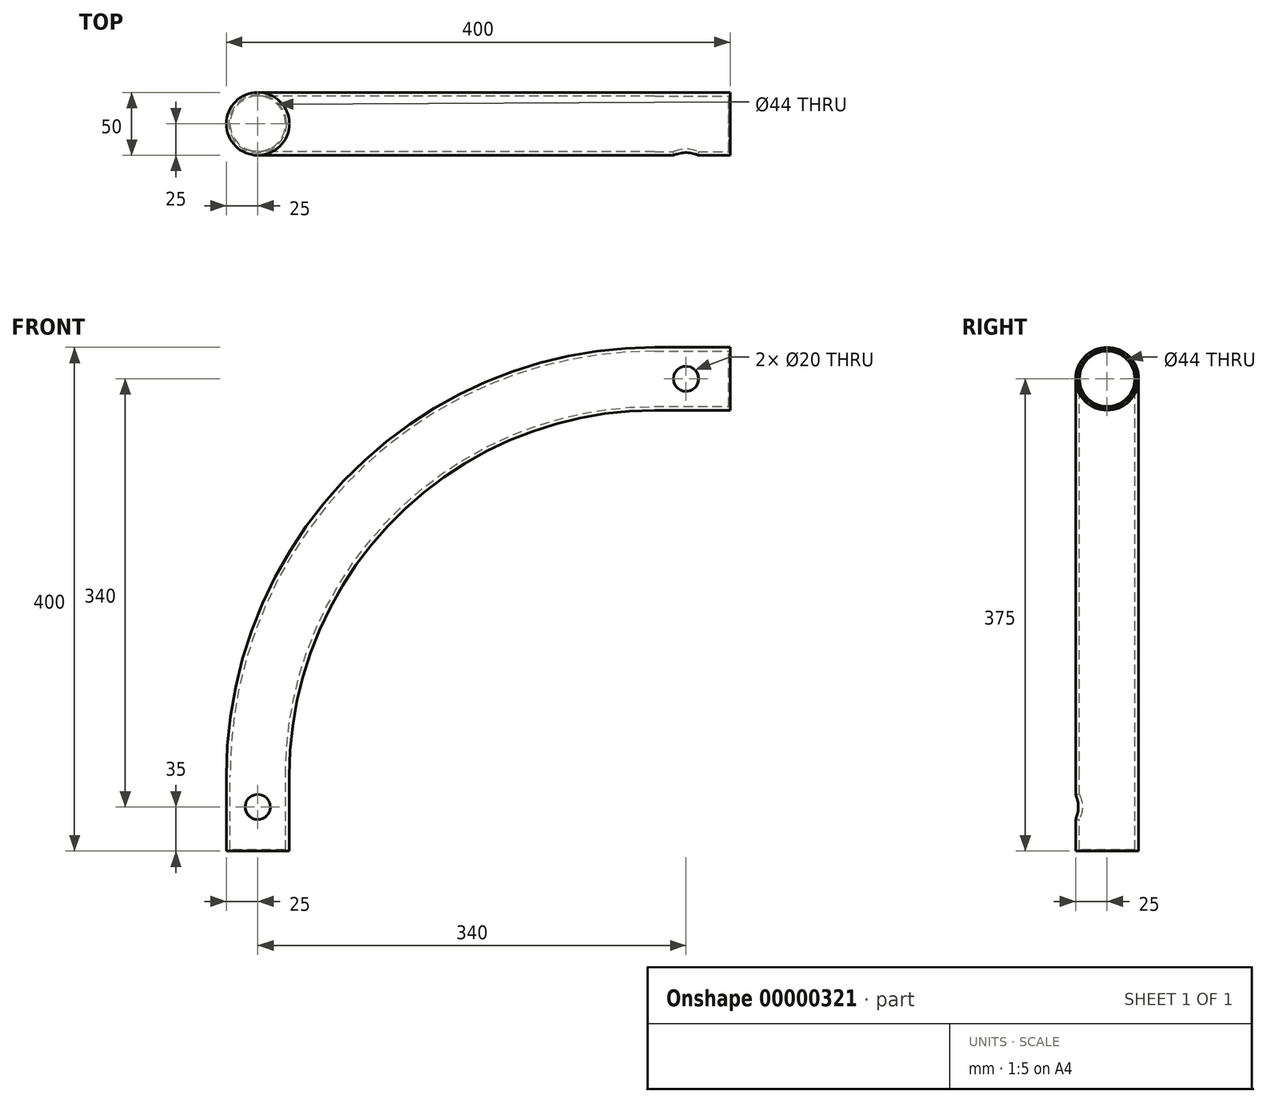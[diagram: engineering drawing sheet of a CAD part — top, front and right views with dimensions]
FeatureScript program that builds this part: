
annotation { "Feature Type Name" : "Feature", "Feature Type Description" : "" }
export const myFeature = defineFeature(function(context is Context, id is Id, definition is map)
    precondition{}
    {
        {
            var Q0;
            Q0   = qCreatedBy(makeId("Top.planeOp"), FACE);
            var sketch = newSketch(context, id + "F0", { "sketchPlane" : qUnion([Q0])});
            skCircle(sketch, "E0", {"center": v(0, 0) * mm, "radius": 25 * mm});
            skSolve(sketch);
        }
        {
            var Q0;
            Q0=qCreatedBy(makeId("Front.planeOp"),FACE);
            var sketch = newSketch(context, id + "F1", { "sketchPlane" : qUnion([Q0])});
            skLineSegment(sketch, "E1", {"start": v(0, 0) * mm, "end": v(0, 60) * mm});
            skLineSegment(sketch, "E2", {"start": v(315, 375) * mm, "end": v(375, 375) * mm});
            skArc(sketch, "E3", {"start": v(315, 375) * mm, "mid": v(92.26, 282.74) * mm, "end": v(0, 60) * mm});
            skSolve(sketch);
        }
        {
            var Q0;
            Q0=makeQuery(id+"F0.imprint","IMPRINT",FACE,{"disambiguationData":[TD([[makeQuery(id+"F0.imprint","IMPRINT",EDGE,{"derivedFrom":sQuery(id+"F0.wireOp",EDGE,"E0")}),1.0]])]});
            var Q1;
            Q1=sQuery(id+"F1.wireOp",EDGE,"E1");
            var Q2;
            Q2=sQuery(id+"F1.wireOp",EDGE,"E3");
            var Q3;
            Q3=sQuery(id+"F1.wireOp",EDGE,"E2");
            sweep(context, id + "F2", {"profiles" : qUnion([Q0]), "path" : qUnion([Q1, Q2, Q3])});
        }
        {
            var Q0;
            Q0=makeQuery(id+"F2.opSweep","CAP_FACE",FACE,{"disambiguationData":[OSD([sQuery(id+"F0.wireOp",EDGE,"E0"),sQuery(id+"F1.wireOp",VERTEX,"E1.start")])],"isStart":true});
            var Q1;
            Q1=makeQuery(id+"F2.opSweep","CAP_FACE",FACE,{"disambiguationData":[OSD([sQuery(id+"F0.wireOp",EDGE,"E0"),sQuery(id+"F1.wireOp",VERTEX,"E2.end")])],"isStart":false});
            cPlane(context, id + "F3", {"entities" : qUnion([Q0, Q1]), "cplaneType" : CPlaneType.MID_PLANE, "offset" : 150 * mm, "width" : 150 * mm, "height" : 150 * mm});
        }
        {
            var Q0;
            Q0=makeQuery(id+"F2.opSweep","CAP_FACE",FACE,{"disambiguationData":[OSD([sQuery(id+"F0.wireOp",EDGE,"E0"),sQuery(id+"F1.wireOp",VERTEX,"E1.start")])],"isStart":true});
            var Q1;
            Q1=makeQuery(id+"F2.opSweep","CAP_FACE",FACE,{"disambiguationData":[OSD([sQuery(id+"F0.wireOp",EDGE,"E0"),sQuery(id+"F1.wireOp",VERTEX,"E2.end")])],"isStart":false});
            shell(context, id + "F4", {"entities" : qUnion([Q0, Q1]), "thickness" : 3 * mm});
        }
        {
            var Q0;
            Q0   = qCreatedBy(makeId("Front.planeOp"), FACE);
            var sketch = newSketch(context, id + "F5", { "sketchPlane" : qUnion([Q0])});
            skCircle(sketch, "E4", {"center": v(0, 35) * mm, "radius": 10 * mm});
            skLineSegment(sketch, "E5.0", {"start": v(-25, 0) * mm, "end": v(25, 0) * mm, "construction": true});
            skSolve(sketch);
        }
        {
            var Q0;
            Q0=makeQuery(id+"F5.imprint","IMPRINT",FACE,{"disambiguationData":[TD([[makeQuery(id+"F5.imprint","IMPRINT",EDGE,{"derivedFrom":sQuery(id+"F5.wireOp",EDGE,"E4")}),1.0]])]});
            extrude(context, id + "F6", {"entities" : qUnion([Q0]), "depth" : 50 * mm});
        }
        {
            var Q0;
            Q0=makeQuery(id+"F6.opExtrude","SWEPT_BODY",BODY,{"disambiguationData":[OSD([sQuery(id+"F5.wireOp",EDGE,"E4")])]});
            var Q1;
            Q1=qCreatedBy(id+"F3.planeOp",FACE);
            mirror(context, id + "F7", {"entities" : qUnion([Q0]), "mirrorPlane" : qUnion([Q1])});
        }
        {
            var Q0;
            Q0=makeQuery(id+"F6.opExtrude","SWEPT_BODY",BODY,{"disambiguationData":[OSD([sQuery(id+"F5.wireOp",EDGE,"E4")])]});
            var Q1;
            Q1=makeQuery(id+"F7.opPattern","COPY",BODY,{"derivedFrom":makeQuery(id+"F6.opExtrude","SWEPT_BODY",BODY,{"disambiguationData":[OSD([sQuery(id+"F5.wireOp",EDGE,"E4")])]}),"instanceName":"1"});
            var Q2;
            Q2=makeQuery(id+"F2.opSweep","SWEPT_BODY",BODY,{"disambiguationData":[OSD([sQuery(id+"F0.wireOp",EDGE,"E0"),sQuery(id+"F1.wireOp",EDGE,"E2")])]});
            booleanBodies(context, id + "F8", {"operationType" : BooleanOperationType.SUBTRACTION, "tools" : qUnion([Q0, Q1]), "targets" : qUnion([Q2])});
        }
        {
            var Q0;
            Q0=makeQuery(id+"F4.opShell","OFFSET_EDGE",EDGE,{"disambiguationData":[OSD([sQuery(id+"F0.wireOp",EDGE,"E0"),sQuery(id+"F1.wireOp",VERTEX,"E1.start")])]});
            var Q1;
            Q1=makeQuery(id+"F4.opShell","OFFSET_EDGE",EDGE,{"disambiguationData":[OSD([sQuery(id+"F0.wireOp",EDGE,"E0"),sQuery(id+"F1.wireOp",VERTEX,"E2.end")])]});
            chamfer(context, id + "F9", {"entities" : qUnion([Q0, Q1]), "width" : 1 * mm, "tangentPropagation" : true});
        }
    });
